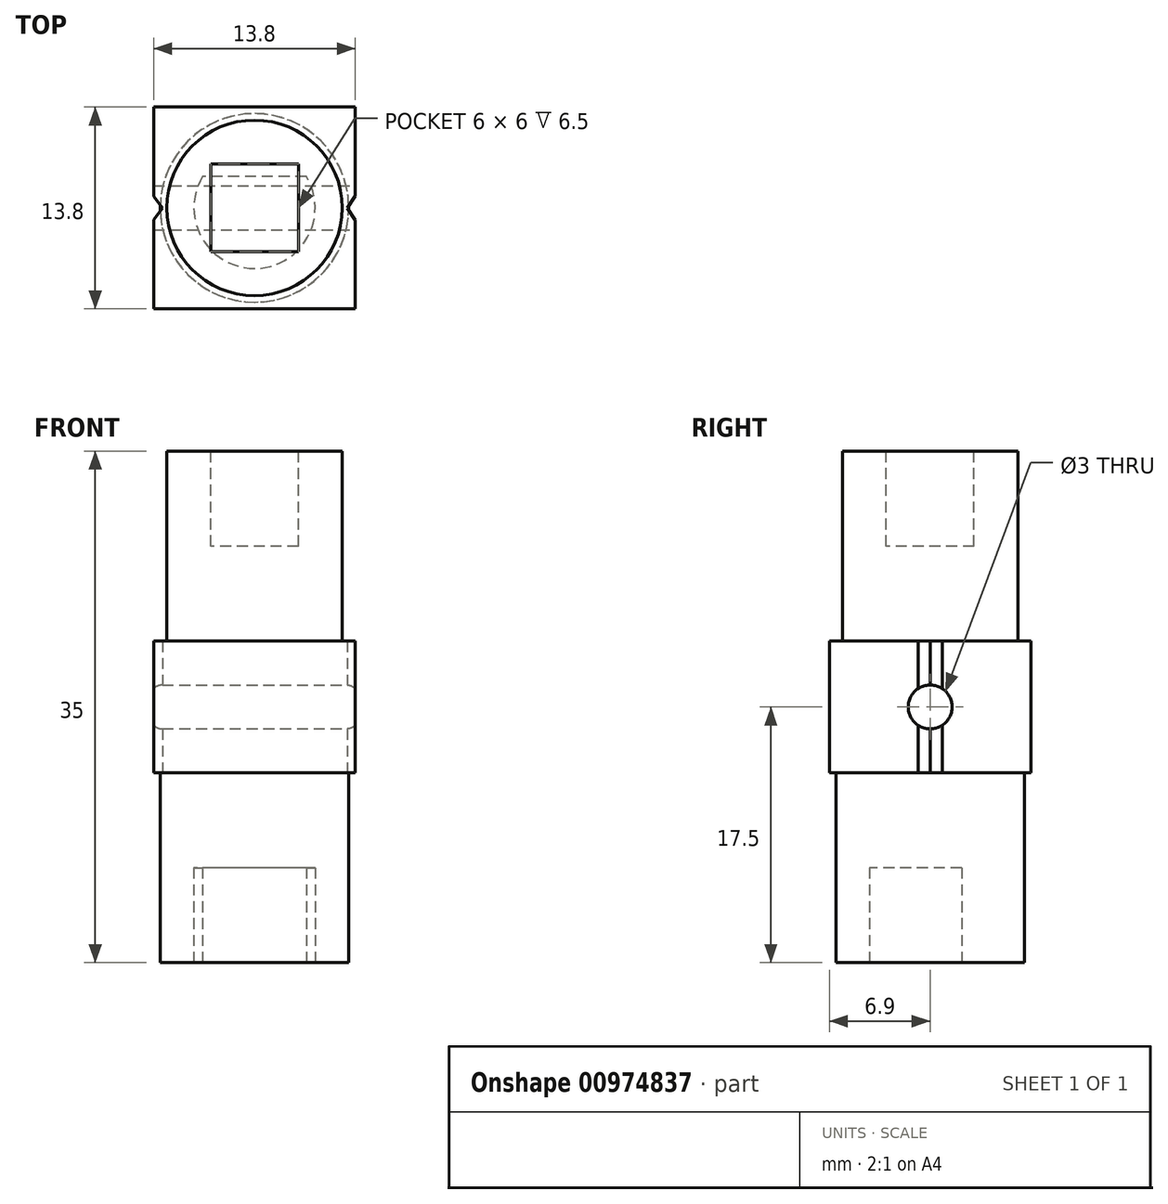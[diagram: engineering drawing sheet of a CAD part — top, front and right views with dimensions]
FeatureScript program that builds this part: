
annotation { "Feature Type Name" : "Feature", "Feature Type Description" : "" }
export const myFeature = defineFeature(function(context is Context, id is Id, definition is map)
    precondition{}
    {
        {
            var Q0;
            Q0=qCreatedBy(makeId("Top.planeOp"),FACE);
            var sketch = newSketch(context, id + "F0", { "sketchPlane" : qUnion([Q0])});
            skLineSegment(sketch, "E0.bottom", {"start": v(6.9, 6.9) * mm, "end": v(-6.9, 6.9) * mm});
            skLineSegment(sketch, "E0.top", {"start": v(6.9, -6.9) * mm, "end": v(-6.9, -6.9) * mm});
            skLineSegment(sketch, "E0.left", {"start": v(6.9, 6.9) * mm, "end": v(6.9, -6.9) * mm});
            skLineSegment(sketch, "E0.right", {"start": v(-6.9, 6.9) * mm, "end": v(-6.9, -6.9) * mm});
            skSolve(sketch);
        }
        {
            var Q0;
            Q0=qSketchRegion(id+"F0",true);
            extrude(context, id + "F1", {"entities" : qUnion([Q0]), "endBound" : BoundingType.SYMMETRIC, "depth" : 9 * mm, "offsetDistance" : 25 * mm});
        }
        {
            var Q0;
            Q0=makeQuery(id+"F1.opExtrude","CAP_FACE",FACE,{"disambiguationData":[OSD([sQuery(id+"F0.wireOp",EDGE,"E0.bottom"),sQuery(id+"F0.wireOp",EDGE,"E0.top"),sQuery(id+"F0.wireOp",EDGE,"E0.left"),sQuery(id+"F0.wireOp",EDGE,"E0.right")])],"isStart":false});
            var sketch = newSketch(context, id + "F2", { "sketchPlane" : qUnion([Q0])});
            skCircle(sketch, "E1", {"center": v(0, 0) * mm, "radius": 6 * mm});
            skSolve(sketch);
        }
        {
            var Q0;
            Q0=qSketchRegion(id+"F2",true);
            extrude(context, id + "F3", {"entities" : qUnion([Q0]), "depth" : 13 * mm, "offsetDistance" : 25 * mm});
        }
        {
            var Q0;
            Q0=makeQuery(id+"F1.opExtrude","CAP_FACE",FACE,{"disambiguationData":[OSD([sQuery(id+"F0.wireOp",EDGE,"E0.bottom"),sQuery(id+"F0.wireOp",EDGE,"E0.top"),sQuery(id+"F0.wireOp",EDGE,"E0.left"),sQuery(id+"F0.wireOp",EDGE,"E0.right")])],"isStart":true});
            var sketch = newSketch(context, id + "F4", { "sketchPlane" : qUnion([Q0])});
            skCircle(sketch, "E2", {"center": v(0, 0) * mm, "radius": 6.45 * mm});
            skSolve(sketch);
        }
        {
            var Q0;
            Q0=qSketchRegion(id+"F4",true);
            extrude(context, id + "F5", {"entities" : qUnion([Q0]), "depth" : 13 * mm, "offsetDistance" : 25 * mm});
        }
        {
            var Q0;
            Q0=makeQuery(id+"F1.opExtrude","SWEPT_FACE",FACE,{"disambiguationData":[OSD([sQuery(id+"F0.wireOp",EDGE,"E0.left")])]});
            var sketch = newSketch(context, id + "F6", { "sketchPlane" : qUnion([Q0])});
            skCircle(sketch, "E3", {"center": v(0, 0) * mm, "radius": 1.5 * mm});
            skSolve(sketch);
        }
        {
            var Q0;
            Q0=qSketchRegion(id+"F6",true);
            extrude(context, id + "F7", {"entities" : qUnion([Q0]), "operationType" : NewBodyOperationType.REMOVE, "endBound" : BoundingType.THROUGH_ALL, "oppositeDirection" : true, "depth" : 25 * mm, "offsetDistance" : 25 * mm});
        }
        {
            var Q0;
            Q0=makeQuery(id+"F1.opExtrude","CAP_FACE",FACE,{"disambiguationData":[OSD([sQuery(id+"F0.wireOp",EDGE,"E0.bottom"),sQuery(id+"F0.wireOp",EDGE,"E0.top"),sQuery(id+"F0.wireOp",EDGE,"E0.left"),sQuery(id+"F0.wireOp",EDGE,"E0.right")])],"isStart":true});
            var sketch = newSketch(context, id + "F8", { "sketchPlane" : qUnion([Q0])});
            skLineSegment(sketch, "E4", {"start": v(6.34, 0) * mm, "end": v(6.9, 0.83) * mm});
            skLineSegment(sketch, "E5", {"start": v(6.34, 0) * mm, "end": v(6.9, -0.83) * mm});
            skLineSegment(sketch, "E6", {"start": v(6.9, 0.83) * mm, "end": v(6.9, -0.83) * mm});
            skLineSegment(sketch, "E7", {"start": v(-6.3, 0) * mm, "end": v(-6.9, 0.8) * mm});
            skLineSegment(sketch, "E8", {"start": v(-6.3, 0) * mm, "end": v(-6.9, -0.8) * mm});
            skLineSegment(sketch, "E9", {"start": v(-6.9, -0.8) * mm, "end": v(-6.9, 0.8) * mm});
            skSolve(sketch);
        }
        {
            var Q0;
            Q0=qSketchRegion(id+"F8",true);
            extrude(context, id + "F9", {"entities" : qUnion([Q0]), "operationType" : NewBodyOperationType.REMOVE, "endBound" : BoundingType.THROUGH_ALL, "oppositeDirection" : true, "depth" : 25 * mm, "offsetDistance" : 25 * mm});
        }
        {
            var Q0;
            Q0=makeQuery(id+"F3.opExtrude","CAP_FACE",FACE,{"disambiguationData":[OSD([sQuery(id+"F2.wireOp",EDGE,"E1")])],"isStart":false});
            var sketch = newSketch(context, id + "F10", { "sketchPlane" : qUnion([Q0])});
            skLineSegment(sketch, "E10.bottom", {"start": v(3, 3) * mm, "end": v(-3, 3) * mm});
            skLineSegment(sketch, "E10.top", {"start": v(3, -3) * mm, "end": v(-3, -3) * mm});
            skLineSegment(sketch, "E10.left", {"start": v(3, 3) * mm, "end": v(3, -3) * mm});
            skLineSegment(sketch, "E10.right", {"start": v(-3, 3) * mm, "end": v(-3, -3) * mm});
            skSolve(sketch);
        }
        {
            var Q0;
            Q0=qSketchRegion(id+"F10",true);
            extrude(context, id + "F11", {"entities" : qUnion([Q0]), "operationType" : NewBodyOperationType.REMOVE, "oppositeDirection" : true, "depth" : 6.5 * mm, "offsetDistance" : 25 * mm});
        }
        {
            var Q0;
            Q0=makeQuery(id+"F5.opExtrude","CAP_FACE",FACE,{"disambiguationData":[OSD([sQuery(id+"F4.wireOp",EDGE,"E2")])],"isStart":false});
            var sketch = newSketch(context, id + "F12", { "sketchPlane" : qUnion([Q0])});
            skCircle(sketch, "E11", {"center": v(0, 0) * mm, "radius": 4.15 * mm});
            skLineSegment(sketch, "E12", {"start": v(0, -2.15) * mm, "end": v(-3.55, -2.15) * mm});
            skLineSegment(sketch, "E13", {"start": v(-3.55, -2.15) * mm, "end": v(3.55, -2.15) * mm});
            skSolve(sketch);
        }
        {
            var Q0;
            {var subQ0=sQuery(id+"F12.wireOp",EDGE,"E13");var subQ4=makeQuery(id+"F12.imprint","IMPRINT",VERTEX,{"derivedFrom":subQ0});Q0=makeQuery(id+"F12.imprint","IMPRINT",FACE,{"disambiguationData":[TD([[makeQuery(id+"F12.imprint","IMPRINT",EDGE,{"disambiguationData":[TD([[subQ4,1.0]])],"derivedFrom":subQ0}),1.0]])]});}
            extrude(context, id + "F13", {"entities" : qUnion([Q0]), "operationType" : NewBodyOperationType.REMOVE, "oppositeDirection" : true, "depth" : 6.5 * mm, "offsetDistance" : 25 * mm});
        }
    });
